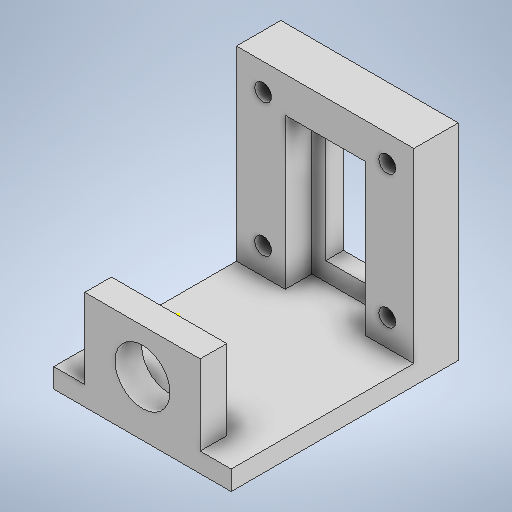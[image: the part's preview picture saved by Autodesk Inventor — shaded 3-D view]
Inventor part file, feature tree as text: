
AUTODESK INVENTOR PART (.ipt)
format: ipt  version: 2025.2 (Build 292293000, 293)  size: 624,128 bytes
history: native  units: mm
features: projected_geometry x22, sketch x20, extrude x19, other x2
ambient origin geometry x8: Origin, YZ Plane, XZ Plane, XY Plane, X Axis, Y Axis, Z Axis, Center Point
bodies: Body1 (feature_tree)
feature tree (63):
  other  "Těleso1"
  extrude  "Vysunutí1"  Depth=18.0mm
  sketch  "Náčrt2"
  sketch  "Náčrt3"
  extrude  "Vysunutí2"  Depth=18.0mm
  extrude  "Vysunutí3"  Depth=20.0mm TaperAngle=0.0deg
  extrude  "Vysunutí4"  Depth=3.4mm
  extrude  "Vysunutí5"  Depth=3.0mm
  extrude  "Vysunutí11"  Depth=1.3mm
  extrude  "Vysunutí12"  Depth=1.3mm
  extrude  "Vysunutí13"  Depth=17.0mm TaperAngle=0.0deg
  extrude  "Vysunutí14"  Depth=6.2mm
  extrude  "Vysunutí15"  Depth=5.0mm
  extrude  "Vysunutí16"  Depth=3.0mm TaperAngle=0.0deg
  sketch  "Náčrt19"
  other  "Pracovní rovina1"
  extrude  "Vysunutí17"  Depth=8.0mm TaperAngle=0.0deg
  extrude  "Vysunutí18"  Depth=5.8mm
  extrude  "Vysunutí19"  Depth=12.0mm
  extrude  "Vysunutí20"  Depth=8.0mm TaperAngle=0.0deg
  extrude  "Vysunutí21"  Depth=20.0mm TaperAngle=0.0deg
  extrude  "Vysunutí22"  Depth=2.5mm
  extrude  "Vysunutí23"  Depth=2.5mm
  extrude  "Vysunutí24"  Depth=5.0mm TaperAngle=0.0deg
  sketch  "Náčrt1"
  projected_geometry  "Promítnutá smyčka1"
  sketch  "Náčrt4"
  sketch  "Náčrt5"
  projected_geometry  "Promítnutá smyčka2"
  projected_geometry  "Promítnutá smyčka3"
  sketch  "Náčrt6"
  projected_geometry  "Promítnutá smyčka4"
  sketch  "Náčrt13"
  projected_geometry  "Promítnutá smyčka10"
  projected_geometry  "Promítnutá smyčka11"
  sketch  "Náčrt14"
  projected_geometry  "Promítnutá smyčka12"
  projected_geometry  "Promítnutá smyčka13"
  sketch  "Náčrt15"
  projected_geometry  "Promítnutá smyčka14"
  sketch  "Náčrt16"
  projected_geometry  "Promítnutá smyčka15"
  sketch  "Náčrt17"
  projected_geometry  "Promítnutá smyčka16"
  sketch  "Náčrt18"
  projected_geometry  "Promítnutá smyčka17"
  projected_geometry  "Promítnutá smyčka18"
  sketch  "Náčrt20"
  sketch  "Náčrt21"
  projected_geometry  "Promítnutá smyčka19"
  sketch  "Náčrt22"
  projected_geometry  "Promítnutá smyčka20"
  projected_geometry  "Promítnutá smyčka21"
  projected_geometry  "Promítnutá smyčka22"
  sketch  "Náčrt23"
  projected_geometry  "Promítnutá smyčka23"
  sketch  "Náčrt24"
  projected_geometry  "Promítnutá smyčka24"
  projected_geometry  "Promítnutá smyčka25"
  sketch  "Náčrt25"
  projected_geometry  "Promítnutá smyčka26"
  sketch  "Náčrt26"
  projected_geometry  "Promítnutá smyčka27"
